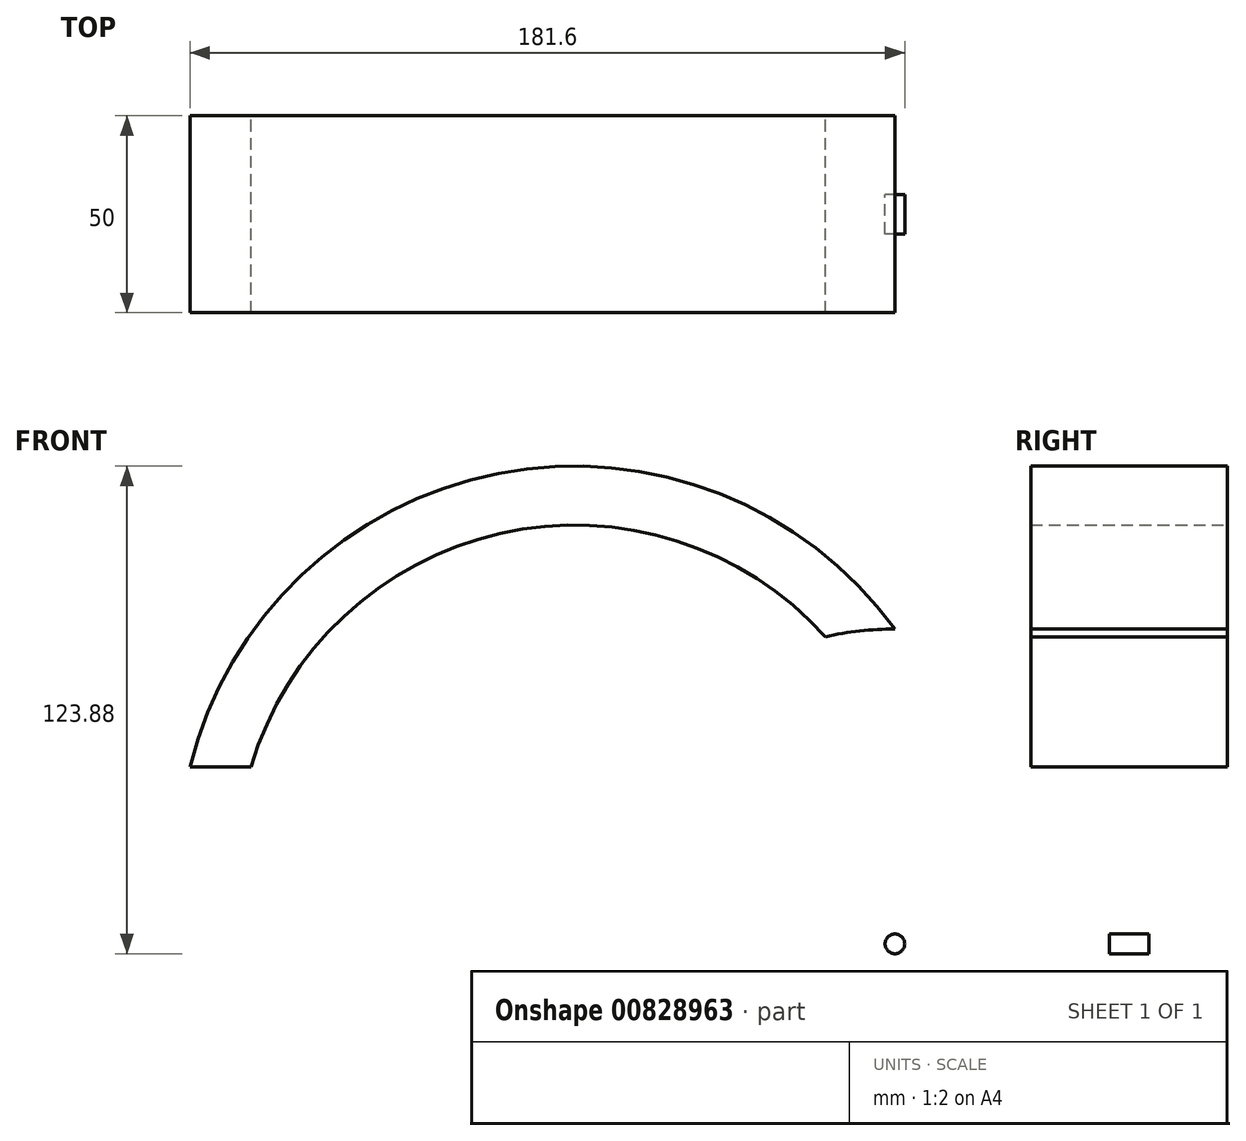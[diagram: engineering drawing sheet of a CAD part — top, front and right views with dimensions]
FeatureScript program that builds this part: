
annotation { "Feature Type Name" : "Feature", "Feature Type Description" : "" }
export const myFeature = defineFeature(function(context is Context, id is Id, definition is map)
    precondition{}
    {
        {
            var Q0;
            Q0=qCreatedBy(makeId("Front.planeOp"),FACE);
            var sketch = newSketch(context, id + "F0", { "sketchPlane" : qUnion([Q0])});
            skCircle(sketch, "E0", {"center": v(0, 0) * mm, "radius": 80 * mm});
            skLineSegment(sketch, "E1", {"start": v(0, 0) * mm, "end": v(0, 45) * mm});
            skLineSegment(sketch, "E2", {"start": v(0, 45) * mm, "end": v(-500, 45) * mm});
            skArc(sketch, "E3", {"start": v(0, 80) * mm, "mid": v(-100.69, 119.51) * mm, "end": v(-179.1, 45) * mm});
            skPoint(sketch, "E3.first.point", {"position": v(0, 80) * mm});
            skPoint(sketch, "E3.second.point", {"position": v(-179.1, 45) * mm});
            skPoint(sketch, "E3.third.point", {"position": v(-138.22, 103.8) * mm});
            skArc(sketch, "E4.0", {"start": v(-12.12, 71.16) * mm, "mid": v(-97.81, 104.79) * mm, "end": v(-164.54, 41.38) * mm});
            skSolve(sketch);
        }
        {
            var Q0;
            {var subQ0=sQuery(id+"F0.wireOp",EDGE,"E3");Q0=makeQuery(id+"F0.imprint","IMPRINT",FACE,{"disambiguationData":[TD([[makeQuery(id+"F0.imprint","IMPRINT",EDGE,{"derivedFrom":subQ0}),1.0]])]});}
            extrude(context, id + "F1", {"entities" : qUnion([Q0]), "endBound" : BoundingType.SYMMETRIC, "depth" : 50 * mm, "offsetDistance" : 25 * mm});
        }
        {
            var Q0;
            Q0=qCreatedBy(makeId("Front.planeOp"),FACE);
            var sketch = newSketch(context, id + "F2", { "sketchPlane" : qUnion([Q0])});
            skCircle(sketch, "E5", {"center": v(0, 0) * mm, "radius": 2.5 * mm});
            skSolve(sketch);
        }
        {
            var Q0;
            Q0=qSketchRegion(id+"F2",true);
            extrude(context, id + "F3", {"entities" : qUnion([Q0]), "endBound" : BoundingType.SYMMETRIC, "depth" : 10 * mm, "offsetDistance" : 25 * mm});
        }
    });
